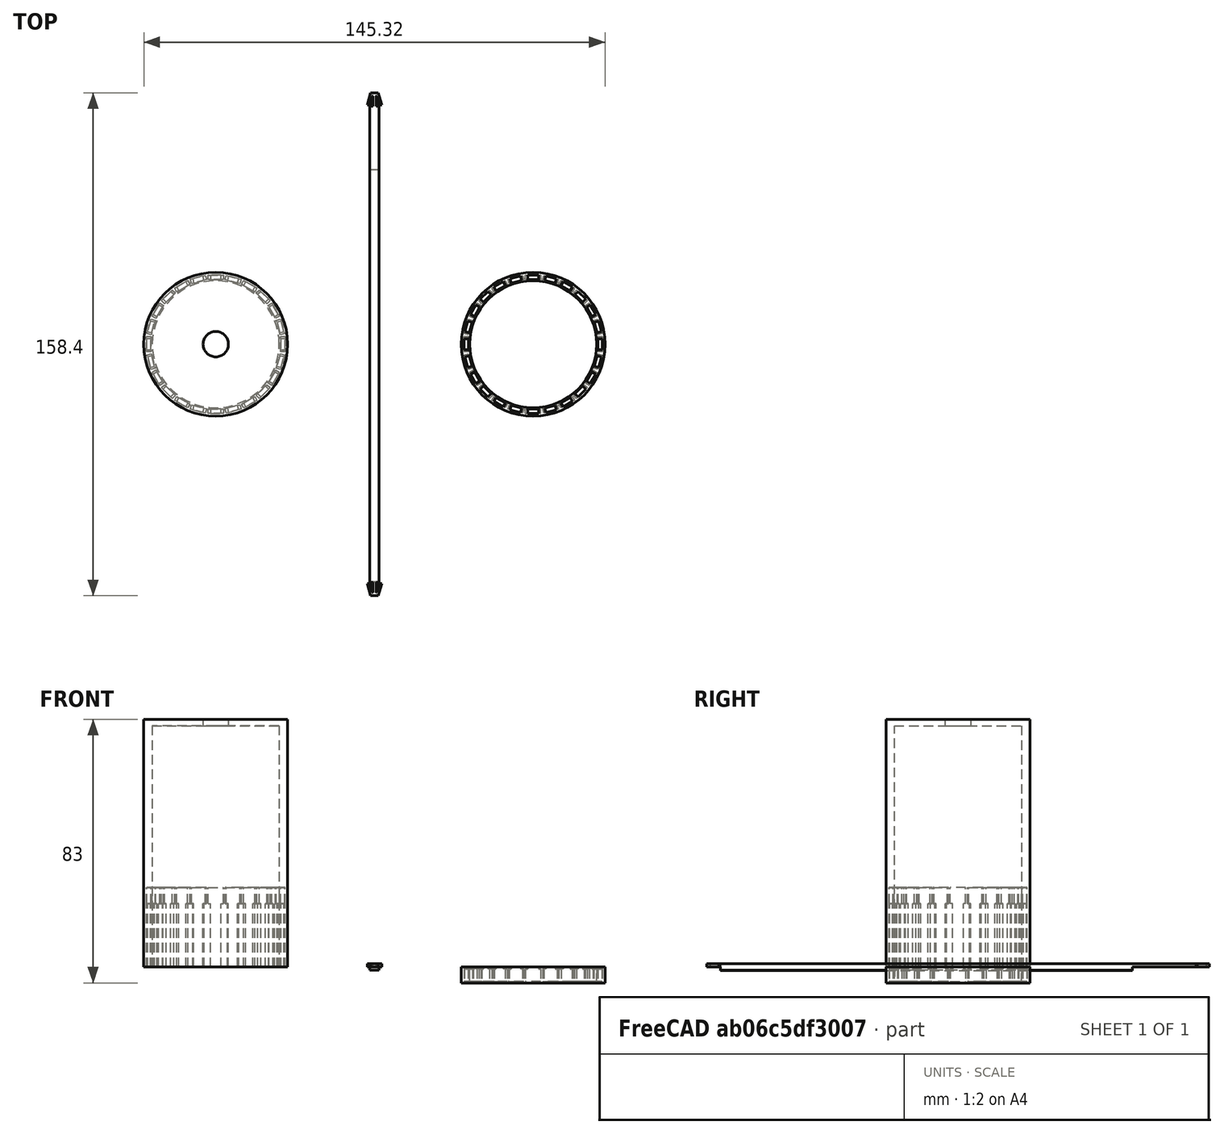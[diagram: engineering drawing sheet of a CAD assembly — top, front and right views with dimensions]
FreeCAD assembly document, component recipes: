
FREECAD ASSEMBLY — COMPONENT RECIPES ("SlenderLamp")

This assembly document has 26 components, labeled P0..P25 below (a component is one placed body or linked part). 26 of them carry a construction recipe — the FreeCAD feature program that regenerates the part from scratch, quoted from this document or its linked companion documents; the rest are supplied as boundary geometry only. No exploded tour is included for this assembly.
COMPONENT P0 — recipe-attached ("Collar001", modeled in this document).
Construction recipe (the document's own serialized feature program — sketch geometry with constraints, then the solid features built on it; lengths are millimeters unless a unit is written):

FEATURE [Sketcher::SketchObject] Sketch001
  ArcFitTolerance = 1e-06
  AttachmentOffset = pos=(0,0,0) rot=(0,0,1;-1.5708rad)
  AttachmentSupport = -> [XY_Plane001]
  FullyConstrained = true
  MakeInternals = false
  MapMode = 5
  Placement = pos=(0,0,0) rot=(0,0,1;4.71239rad)
  sketch-geometry (13):
    g0: Circle CenterX=0 CenterY=0 CenterZ=0 NormalX=0 NormalY=0 NormalZ=1 AngleXU=0 Radius=20
    g1: Circle CenterX=0 CenterY=0 CenterZ=0 NormalX=0 NormalY=0 NormalZ=1 AngleXU=0 Radius=22.6638
    g2: LineSegment StartX=20.4 StartY=1.7 StartZ=0 EndX=20.4 EndY=-1.7 EndZ=0
    g3: LineSegment StartX=20.4 StartY=-1.7 StartZ=0 EndX=21.8 EndY=-1.7 EndZ=0
    g4: LineSegment StartX=21.8 StartY=-1.7 StartZ=0 EndX=21.8 EndY=1.7 EndZ=0
    g5: LineSegment StartX=21.8 StartY=1.7 StartZ=0 EndX=20.4 EndY=1.7 EndZ=0
    g6: LineSegment [constr] StartX=21.8 StartY=1.7 StartZ=0 EndX=22.6 EndY=1.7 EndZ=0
    g7: LineSegment StartX=20.4 StartY=1.7 StartZ=0 EndX=20.4 EndY=2.4 EndZ=0
    g8: LineSegment StartX=20.4 StartY=2.4 StartZ=0 EndX=21.8 EndY=2.4 EndZ=0
    g9: LineSegment StartX=21.8 StartY=2.4 StartZ=0 EndX=21.8 EndY=1.7 EndZ=0
    g10: LineSegment StartX=21.8 StartY=-1.7 StartZ=0 EndX=21.8 EndY=-2.4 EndZ=0
    g11: LineSegment StartX=21.8 StartY=-2.4 StartZ=0 EndX=20.4 EndY=-2.4 EndZ=0
    g12: LineSegment StartX=20.4 StartY=-2.4 StartZ=0 EndX=20.4 EndY=-1.7 EndZ=0
  constraints (34):
    c: Diameter(g0) = 40
    c: Coincident(g0,g-1)
    c: Coincident(g1,g0)
    c: Coincident(g2,g3)
    c: Coincident(g3,g4)
    c: Coincident(g4,g5)
    c: Coincident(g5,g2)
    c: Vertical(g4)
    c: Horizontal(g3)
    c: Horizontal(g5)
    c: Distance(g0,g2) = 0.4
    c: Coincident(g6,g4)
    c: PointOnObject(g6,g1)
    c: Horizontal(g6)
    c: Distance(g6,g6) = 0.8
    c: Distance(g3,g3) = 1.4
    c: Symmetric(g2,g2,g-1)
    c: DistanceY(g2,g2) = 3.4
    c: Coincident(g7,g2)
    c: Vertical(g7)
    c: Coincident(g8,g7)
    c: Horizontal(g8)
    c: Coincident(g9,g8)
    c: Coincident(g9,g4)
    c: Vertical(g9)
    c: Coincident(g10,g3)
    c: Vertical(g10)
    c: Coincident(g11,g10)
    c: Horizontal(g11)
    c: Coincident(g12,g11)
    c: Coincident(g12,g2)
    c: Vertical(g12)
    c: Equal(g12,g7)
    c: DistanceY(g11,g7) = 4.8
FEATURE [PartDesign::Pad] Pad001
  Direction = (0,0,1)
  Length = 5
  Length2 = 10
  Profile = -> Sketch001 [Edge1,Edge2]
  ReferenceAxis = -> Sketch001 [N_Axis]
  Refine = true
  Reversed = true
  Suppressed = false
  Type = 0
FEATURE [PartDesign::Pocket] Pocket
  BaseFeature = -> Pad001
  Direction = (0,0,-1)
  Length = 0
  Length2 = 5
  Offset = -0.4
  Profile = -> Sketch001 [Edge4,Edge3,Edge8,Edge9]
  ReferenceAxis = -> Sketch001 [N_Axis]
  Refine = true
  Suppressed = false
  Type = 3
  UpToFace = -> Pad001 [Face4]
FEATURE [PartDesign::SubShapeBinder] Binder
  BindCopyOnChange = 0
  BindMode = 0
  ClaimChildren = false
  Context = -> Body001 [Binder.]
  Fuse = false
  MakeFace = true
  OffsetFill = false
  OffsetIntersection = false
  OffsetJoinType = 0
  OffsetOpenResult = false
  PartialLoad = false
  Placement = pos=(0,0,-0.6) rot=(0,0,1;0rad)
  Refine = true
  Relative = true
  Support = -> [Sketch001[Edge5,Edge6,Edge7,Edge8,Edge3,Edge10,Edge11,Edge12]]
  _Version = 2
FEATURE [PartDesign::Pocket] Pocket001
  BaseFeature = -> Pocket
  Direction = (0,0,-1)
  Length = 0
  Length2 = 5
  Profile = -> Binder
  Refine = true
  Suppressed = false
  Type = 3
  UpToFace = -> Pocket [Face9]
FEATURE [PartDesign::PolarPattern] PolarPattern
  Angle = 360
  Axis = -> Sketch001 [N_Axis]
  BaseFeature = -> Pocket001
  Mode = 0
  Occurrences = 24
  Offset = 120
  Originals = -> [Pocket,Pocket001]
  Refine = true
  Suppressed = false
  TransformMode = 0
FEATURE [PartDesign::Body] Body001  label="Bottom"
  AllowCompound = false
  Group = -> [Sketch001,Pad001,Pocket,Binder,Pocket001,PolarPattern]
  Origin = -> Origin001
  Placement = pos=(250,0,0) rot=(0,0,1;0rad)
  Tip = -> PolarPattern
COMPONENT P1 — recipe-attached ("Pillar001", modeled in this document).
Construction recipe (the document's own serialized feature program — sketch geometry with constraints, then the solid features built on it; lengths are millimeters unless a unit is written):

FEATURE [Sketcher::SketchObject] Sketch
  ArcFitTolerance = 1e-06
  AttachmentSupport = -> [XY_Plane]
  FullyConstrained = false
  MakeInternals = false
  MapMode = 5
  expr: Constraints[29] = 65 mm + 20 mm / 2
  sketch-geometry (11):
    g0: LineSegment StartX=0 StartY=0 StartZ=0 EndX=0 EndY=79.2 EndZ=0
    g1: LineSegment StartX=0 StartY=79.2 StartZ=0 EndX=1.237 EndY=79.2 EndZ=0
    g2: LineSegment StartX=0.5 StartY=78.1 StartZ=0 EndX=0.5 EndY=75 EndZ=0
    g3: LineSegment StartX=0 StartY=0 StartZ=0 EndX=1.5 EndY=0 EndZ=0
    g4: LineSegment StartX=0.5 StartY=75 StartZ=0 EndX=1.5 EndY=75 EndZ=0
    g5: LineSegment StartX=1.5 StartY=75 StartZ=0 EndX=1.5 EndY=0 EndZ=0
    g6: ArcOfCircle CenterX=0.6 CenterY=78.1 CenterZ=0 NormalX=0 NormalY=0 NormalZ=1 AngleXU=0 Radius=0.1 StartAngle=0.261799 EndAngle=3.14159
    g7: LineSegment StartX=2.27228 StartY=75.3363 StartZ=0 EndX=1.237 EndY=79.2 EndZ=0
    g8: LineSegment StartX=1.44406 StartY=75.3363 StartZ=0 EndX=0.696593 EndY=78.1259 EndZ=0
    g9: LineSegment [constr] StartX=0.359783 StartY=78.2 StartZ=0 EndX=1.0954 EndY=78.2 EndZ=0
    g10: LineSegment StartX=1.44406 StartY=75.3363 StartZ=0 EndX=2.27228 EndY=75.3363 EndZ=0
  constraints (30):
    c: Coincident(g0,g-1)
    c: Coincident(g3,g0)
    c: Horizontal(g1)
    c: PointOnObject(g3,g-1)
    c: Horizontal(g4)
    c: Coincident(g5,g4)
    c: Coincident(g5,g3)
    c: Vertical(g5)
    c: Distance(g3,g3) = 1.5
    c: Coincident(g2,g4)
    c: Distance(g4,g4) = 1
    c: Perpendicular(g2,g4)
    c: Coincident(g7,g1)
    c: Tangent(g8,g6) = -1.5708
    c: Tangent(g6,g2) = -1.5708
    c: Parallel(g8,g7)
    c: Diameter(g6) = 0.2
    c: Horizontal(g9)
    c: Tangent(g9,g6)
    c: Distance(g1,g9) = 1
    c: PointOnObject(g0,g-2)
    c: Coincident(g10,g8)
    c: Coincident(g10,g7)
    c: Coincident(g1,g0)
    c: DistanceY(g2,g0) = 4.2
    c: Distance(g7,g7) = 4
    c: Angle(g7,g10) = 1.309
    c: Horizontal(g10)
    c: Distance(g8,g7) = 0.8
    c: DistanceY(g5,g5) = 75
FEATURE [PartDesign::Pad] Pad
  Direction = (0,0,1)
  Length = 1
  Length2 = 10
  Profile = -> Sketch
  ReferenceAxis = -> Sketch [N_Axis]
  Refine = true
  Suppressed = false
  Type = 0
FEATURE [PartDesign::Mirrored] Mirrored
  MirrorPlane = -> Sketch [V_Axis]
  Refine = true
  Suppressed = false
  TransformMode = 0
FEATURE [PartDesign::Mirrored] Mirrored001
  MirrorPlane = -> Sketch [H_Axis]
  Refine = true
  Suppressed = false
  TransformMode = 0
FEATURE [PartDesign::MultiTransform] MultiTransform
  BaseFeature = -> Pad
  Originals = -> [Pad]
  Refine = true
  Suppressed = false
  TransformMode = 0
  Transformations = -> [Mirrored,Mirrored001]
FEATURE [Sketcher::SketchObject] Sketch003
  ArcFitTolerance = 1e-06
  AttachmentSupport = -> [XZ_Plane]
  ExternalGeometry = -> [MultiTransform]
  FullyConstrained = true
  MakeInternals = false
  MapMode = 5
  Placement = pos=(0,0,0) rot=(1,0,0;1.5708rad)
  sketch-geometry (4):
    g0: ArcOfCircle CenterX=0 CenterY=21.6103 CenterZ=0 NormalX=0 NormalY=0 NormalZ=1 AngleXU=0 Radius=22.66 StartAngle=4.64614 EndAngle=4.77863
    g1: LineSegment StartX=1.5 StartY=-1 StartZ=0 EndX=1.5 EndY=0 EndZ=0
    g2: LineSegment StartX=-1.5 StartY=0 StartZ=0 EndX=-1.5 EndY=-1 EndZ=0
    g3: LineSegment StartX=-1.5 StartY=0 StartZ=0 EndX=1.5 EndY=0 EndZ=0
  constraints (13):
    c: PointOnObject(g0,g-2)
    c: Coincident(g1,g0)
    c: PointOnObject(g1,g-1)
    c: PointOnObject(g2,g-1)
    c: PointOnObject(g2,g-5)
    c: PointOnObject(g1,g-6)
    c: Coincident(g2,g0)
    c: PointOnObject(g0,g-5)
    c: PointOnObject(g0,g-6)
    c: Radius(g0) = 22.66
    c: Distance(g2) = 1
    c: Coincident(g3,g2)
    c: Coincident(g3,g1)
FEATURE [PartDesign::Pad] Pad003
  BaseFeature = -> MultiTransform
  Direction = (0,-1,2e-16)
  Length = 74.8
  Length2 = 55
  Profile = -> Sketch003
  ReferenceAxis = -> Sketch003 [N_Axis]
  Refine = true
  Suppressed = false
  Type = 4
FEATURE [PartDesign::Body] Body  label="Connector"
  AllowCompound = false
  Group = -> [Sketch,Pad,MultiTransform,Mirrored,Mirrored001,Sketch003,Pad003]
  Origin = -> Origin
  Placement = pos=(200,0,0) rot=(1,0,0;0rad)
  Tip = -> Pad003
COMPONENT P2 — same part as P1; its construction recipe is shown at P1.
COMPONENT P3 — same part as P1; its construction recipe is shown at P1.
COMPONENT P4 — same part as P1; its construction recipe is shown at P1.
COMPONENT P5 — same part as P1; its construction recipe is shown at P1.
COMPONENT P6 — same part as P1; its construction recipe is shown at P1.
COMPONENT P7 — same part as P1; its construction recipe is shown at P1.
COMPONENT P8 — same part as P1; its construction recipe is shown at P1.
COMPONENT P9 — same part as P1; its construction recipe is shown at P1.
COMPONENT P10 — same part as P1; its construction recipe is shown at P1.
COMPONENT P11 — same part as P1; its construction recipe is shown at P1.
COMPONENT P12 — same part as P1; its construction recipe is shown at P1.
COMPONENT P13 — same part as P1; its construction recipe is shown at P1.
COMPONENT P14 — same part as P1; its construction recipe is shown at P1.
COMPONENT P15 — same part as P1; its construction recipe is shown at P1.
COMPONENT P16 — same part as P1; its construction recipe is shown at P1.
COMPONENT P17 — same part as P1; its construction recipe is shown at P1.
COMPONENT P18 — same part as P1; its construction recipe is shown at P1.
COMPONENT P19 — same part as P1; its construction recipe is shown at P1.
COMPONENT P20 — same part as P1; its construction recipe is shown at P1.
COMPONENT P21 — same part as P1; its construction recipe is shown at P1.
COMPONENT P22 — same part as P1; its construction recipe is shown at P1.
COMPONENT P23 — same part as P1; its construction recipe is shown at P1.
COMPONENT P24 — same part as P1; its construction recipe is shown at P1.
COMPONENT P25 — recipe-attached ("Top001", modeled in this document).
Construction recipe (the document's own serialized feature program — sketch geometry with constraints, then the solid features built on it; lengths are millimeters unless a unit is written):

FEATURE [Sketcher::SketchObject] Sketch002
  ArcFitTolerance = 1e-06
  AttachmentOffset = pos=(0,0,0) rot=(0,0,1;-1.5708rad)
  FullyConstrained = true
  MakeInternals = false
  MapMode = 5
  Placement = pos=(0,0,0) rot=(0,0,1;4.71239rad)
  sketch-geometry (14):
    g0: Circle CenterX=0 CenterY=0 CenterZ=0 NormalX=0 NormalY=0 NormalZ=1 AngleXU=0 Radius=20
    g1: Circle CenterX=0 CenterY=0 CenterZ=0 NormalX=0 NormalY=0 NormalZ=1 AngleXU=0 Radius=22.6638
    g2: LineSegment StartX=20.4 StartY=1.7 StartZ=0 EndX=20.4 EndY=-1.7 EndZ=0
    g3: LineSegment StartX=20.4 StartY=-1.7 StartZ=0 EndX=21.8 EndY=-1.7 EndZ=0
    g4: LineSegment StartX=21.8 StartY=-1.7 StartZ=0 EndX=21.8 EndY=1.7 EndZ=0
    g5: LineSegment StartX=21.8 StartY=1.7 StartZ=0 EndX=20.4 EndY=1.7 EndZ=0
    g6: LineSegment [constr] StartX=21.8 StartY=1.7 StartZ=0 EndX=22.6 EndY=1.7 EndZ=0
    g7: LineSegment StartX=20.4 StartY=1.7 StartZ=0 EndX=20.4 EndY=2.4 EndZ=0
    g8: LineSegment StartX=20.4 StartY=2.4 StartZ=0 EndX=21.8 EndY=2.4 EndZ=0
    g9: LineSegment StartX=21.8 StartY=2.4 StartZ=0 EndX=21.8 EndY=1.7 EndZ=0
    g10: LineSegment StartX=21.8 StartY=-1.7 StartZ=0 EndX=21.8 EndY=-2.4 EndZ=0
    g11: LineSegment StartX=21.8 StartY=-2.4 StartZ=0 EndX=20.4 EndY=-2.4 EndZ=0
    g12: LineSegment StartX=20.4 StartY=-2.4 StartZ=0 EndX=20.4 EndY=-1.7 EndZ=0
    g13: Circle CenterX=0 CenterY=0 CenterZ=0 NormalX=0 NormalY=0 NormalZ=1 AngleXU=0 Radius=4
  constraints (36):
    c: Diameter(g0) = 40
    c: Coincident(g0,g-1)
    c: Coincident(g1,g0)
    c: Coincident(g2,g3)
    c: Coincident(g3,g4)
    c: Coincident(g4,g5)
    c: Coincident(g5,g2)
    c: Vertical(g4)
    c: Horizontal(g3)
    c: Horizontal(g5)
    c: Distance(g0,g2) = 0.4
    c: Coincident(g6,g4)
    c: PointOnObject(g6,g1)
    c: Horizontal(g6)
    c: Distance(g6,g6) = 0.8
    c: Distance(g3,g3) = 1.4
    c: Symmetric(g2,g2,g-1)
    c: DistanceY(g2,g2) = 3.4
    c: Coincident(g7,g2)
    c: Vertical(g7)
    c: Coincident(g8,g7)
    c: Horizontal(g8)
    c: Coincident(g9,g8)
    c: Coincident(g9,g4)
    c: Vertical(g9)
    c: Coincident(g10,g3)
    c: Vertical(g10)
    c: Coincident(g11,g10)
    c: Horizontal(g11)
    c: Coincident(g12,g11)
    c: Coincident(g12,g2)
    c: Vertical(g12)
    c: Equal(g12,g7)
    c: DistanceY(g11,g7) = 4.8
    c: Diameter(g13) = 8
    c: Coincident(g13,g0)
FEATURE [PartDesign::Pad] Pad002
  Direction = (0,0,1)
  Length = 78
  Length2 = 10
  Placement = pos=(0,0,0) rot=(0,0,1;4.71239rad)
  Profile = -> Sketch002 [Edge2,Edge13]
  ReferenceAxis = -> Sketch002 [N_Axis]
  Refine = true
  Suppressed = false
  Type = 0
FEATURE [PartDesign::Pocket] Pocket002
  BaseFeature = -> Pad002
  Direction = (0,0,-1)
  Length = 0
  Length2 = 5
  Offset = -2
  Placement = pos=(0,0,0) rot=(0,0,1;4.71239rad)
  Profile = -> Sketch002 [Edge1]
  ReferenceAxis = -> Sketch002 [N_Axis]
  Refine = true
  Suppressed = false
  Type = 3
  UpToFace = -> Pad002 [Face4]
FEATURE [PartDesign::SubShapeBinder] Binder001
  BindCopyOnChange = 0
  BindMode = 0
  ClaimChildren = false
  Context = -> Body002 [Binder001.]
  Fuse = false
  MakeFace = true
  OffsetFill = false
  OffsetIntersection = false
  OffsetJoinType = 0
  OffsetOpenResult = false
  PartialLoad = false
  Placement = pos=(0,0,20) rot=(0,0,1;0rad)
  Refine = true
  Relative = true
  Support = -> [Sketch002[Edge11,Edge12,Edge10,Edge3,Edge8,Edge7,Edge5,Edge6]]
  _Version = 2
FEATURE [PartDesign::Pocket] Pocket003
  BaseFeature = -> Pocket002
  Direction = (0,0,-1)
  Length = 20
  Length2 = 5
  Placement = pos=(0,0,0) rot=(0,0,1;4.71239rad)
  Profile = -> Sketch002 [Edge3,Edge4,Edge8,Edge9]
  ReferenceAxis = -> Sketch002 [N_Axis]
  Refine = true
  Reversed = true
  Suppressed = false
  Type = 0
FEATURE [PartDesign::Pocket] Pocket004
  BaseFeature = -> Pocket003
  Direction = (0,0,-1)
  Length = 5
  Length2 = 5
  Placement = pos=(0,0,0) rot=(0,0,1;4.71239rad)
  Profile = -> Binder001
  Refine = true
  Reversed = true
  Suppressed = false
  Type = 0
FEATURE [PartDesign::PolarPattern] PolarPattern001
  Angle = 360
  Axis = -> Sketch002 [N_Axis]
  BaseFeature = -> Pocket004
  Mode = 0
  Occurrences = 24
  Offset = 120
  Originals = -> [Pocket003,Pocket004]
  Placement = pos=(0,0,0) rot=(0,0,1;4.71239rad)
  Refine = true
  Suppressed = false
  TransformMode = 0
FEATURE [PartDesign::Body] Body002  label="Top"
  AllowCompound = false
  Group = -> [Sketch002,Pad002,Pocket002,Binder001,Pocket003,Pocket004,PolarPattern001]
  Origin = -> Origin003
  Placement = pos=(150,0,0) rot=(0,0,1;0rad)
  Tip = -> PolarPattern001
PROVENANCE & LICENSES
A FreeCAD (.FCStd) document from a public repository crawl; recipes are the document's own serialized feature recipes (and, for linked parts, companion documents' recipes).
License: as declared in the source repository (recorded in the dataset sidecar).
